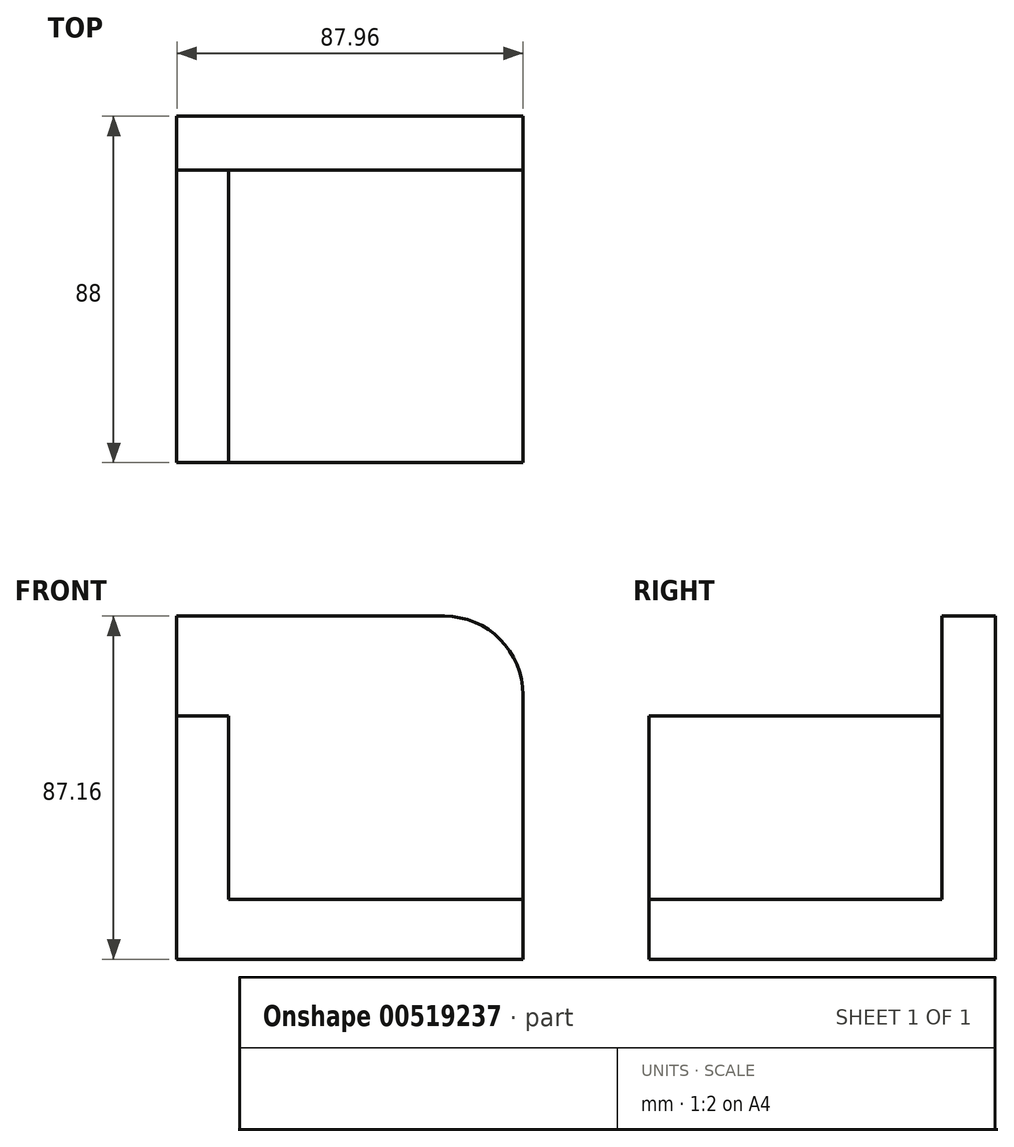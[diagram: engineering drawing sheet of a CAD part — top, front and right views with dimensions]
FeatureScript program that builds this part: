
annotation { "Feature Type Name" : "Feature", "Feature Type Description" : "" }
export const myFeature = defineFeature(function(context is Context, id is Id, definition is map)
    precondition{}
    {
        {
            var Q0;
            Q0=qCreatedBy(makeId("Front.planeOp"),FACE);
            var sketch = newSketch(context, id + "F0", { "sketchPlane" : qUnion([Q0])});
            skLineSegment(sketch, "E0.bottom", {"start": v(43.98, 43.58) * mm, "end": v(-43.98, 43.58) * mm});
            skLineSegment(sketch, "E0.top", {"start": v(43.98, -43.58) * mm, "end": v(-43.98, -43.58) * mm});
            skLineSegment(sketch, "E0.left", {"start": v(43.98, 43.58) * mm, "end": v(43.98, -43.58) * mm});
            skLineSegment(sketch, "E0.right", {"start": v(-43.98, 43.58) * mm, "end": v(-43.98, -43.58) * mm});
            skPoint(sketch, "E0.middle", {"position": v(0, 0) * mm});
            skSolve(sketch);
        }
        {
            var Q0;
            Q0=makeQuery(id+"F0.imprint","IMPRINT",FACE,{"disambiguationData":[TD([[makeQuery(id+"F0.imprint","IMPRINT",EDGE,{"derivedFrom":sQuery(id+"F0.wireOp",EDGE,"E0.bottom")}),1.0]])]});
            extrude(context, id + "F1", {"entities" : qUnion([Q0]), "endBound" : BoundingType.SYMMETRIC, "depth" : 88 * mm, "offsetDistance" : 25 * mm});
        }
        {
            var Q0;
            Q0=makeQuery(id+"F1.opExtrude","SWEPT_FACE",FACE,{"disambiguationData":[OSD([sQuery(id+"F0.wireOp",EDGE,"E0.bottom")])]});
            var sketch = newSketch(context, id + "F2", { "sketchPlane" : qUnion([Q0])});
            skLineSegment(sketch, "E1.bottom", {"start": v(43.98, -44) * mm, "end": v(-30.83, -44) * mm});
            skLineSegment(sketch, "E1.top", {"start": v(43.98, 30.36) * mm, "end": v(-30.83, 30.36) * mm});
            skLineSegment(sketch, "E1.left", {"start": v(43.98, -44) * mm, "end": v(43.98, 30.36) * mm});
            skLineSegment(sketch, "E1.right", {"start": v(-30.83, -44) * mm, "end": v(-30.83, 30.36) * mm});
            skSolve(sketch);
        }
        {
            var Q0;
            Q0=makeQuery(id+"F2.imprint","IMPRINT",FACE,{"disambiguationData":[TD([[makeQuery(id+"F2.imprint","IMPRINT",EDGE,{"derivedFrom":sQuery(id+"F2.wireOp",EDGE,"E1.bottom")}),-1.0]])]});
            extrude(context, id + "F3", {"entities" : qUnion([Q0]), "operationType" : NewBodyOperationType.REMOVE, "oppositeDirection" : true, "depth" : 72 * mm, "offsetDistance" : 25 * mm});
        }
        {
            var Q0;
            Q0=makeQuery(id+"F3.boolean.opBoolean","COPY",FACE,{"derivedFrom":makeQuery(id+"F3.opExtrude","SWEPT_FACE",FACE,{"disambiguationData":[OSD([sQuery(id+"F2.wireOp",EDGE,"E1.right")])]})});
            var sketch = newSketch(context, id + "F4", { "sketchPlane" : qUnion([Q0])});
            skLineSegment(sketch, "E2.bottom", {"start": v(30.36, 43.58) * mm, "end": v(-44, 43.58) * mm});
            skLineSegment(sketch, "E2.top", {"start": v(30.36, 18.25) * mm, "end": v(-44, 18.25) * mm});
            skLineSegment(sketch, "E2.left", {"start": v(30.36, 43.58) * mm, "end": v(30.36, 18.25) * mm});
            skLineSegment(sketch, "E2.right", {"start": v(-44, 43.58) * mm, "end": v(-44, 18.25) * mm});
            skSolve(sketch);
        }
        {
            var Q0;
            Q0=makeQuery(id+"F4.imprint","IMPRINT",FACE,{"disambiguationData":[TD([[makeQuery(id+"F4.imprint","IMPRINT",EDGE,{"derivedFrom":sQuery(id+"F4.wireOp",EDGE,"E2.bottom")}),-1.0]])]});
            extrude(context, id + "F5", {"entities" : qUnion([Q0]), "operationType" : NewBodyOperationType.REMOVE, "endBound" : BoundingType.THROUGH_ALL, "oppositeDirection" : true, "depth" : 25 * mm, "offsetDistance" : 25 * mm});
        }
        {
            var Q0;
            Q0=makeQuery(id+"F1.opExtrude","SWEPT_EDGE",EDGE,{"disambiguationData":[OSD([sQuery(id+"F0.wireOp",EDGE,"E0.bottom"),sQuery(id+"F0.wireOp",EDGE,"E0.left")])]});
            var Q1;
            Q1=makeQuery(id+"F5.boolean.opBoolean","COPY",EDGE,{"derivedFrom":makeQuery(id+"F5.opExtrude","SWEPT_EDGE",EDGE,{"disambiguationData":[OSD([sQuery(id+"F0.wireOp",EDGE,"E0.bottom"),sQuery(id+"F2.wireOp",EDGE,"E1.bottom"),sQuery(id+"F2.wireOp",EDGE,"E1.right"),sQuery(id+"F4.wireOp",EDGE,"E2.top"),sQuery(id+"F4.wireOp",EDGE,"E2.right")])]})});
            fillet(context, id + "F6", {"entities" : qUnion([Q0, Q1]), "radius" : 20 * mm, "tangentPropagation" : true, "allowEdgeOverflow" : false});
        }
    });
